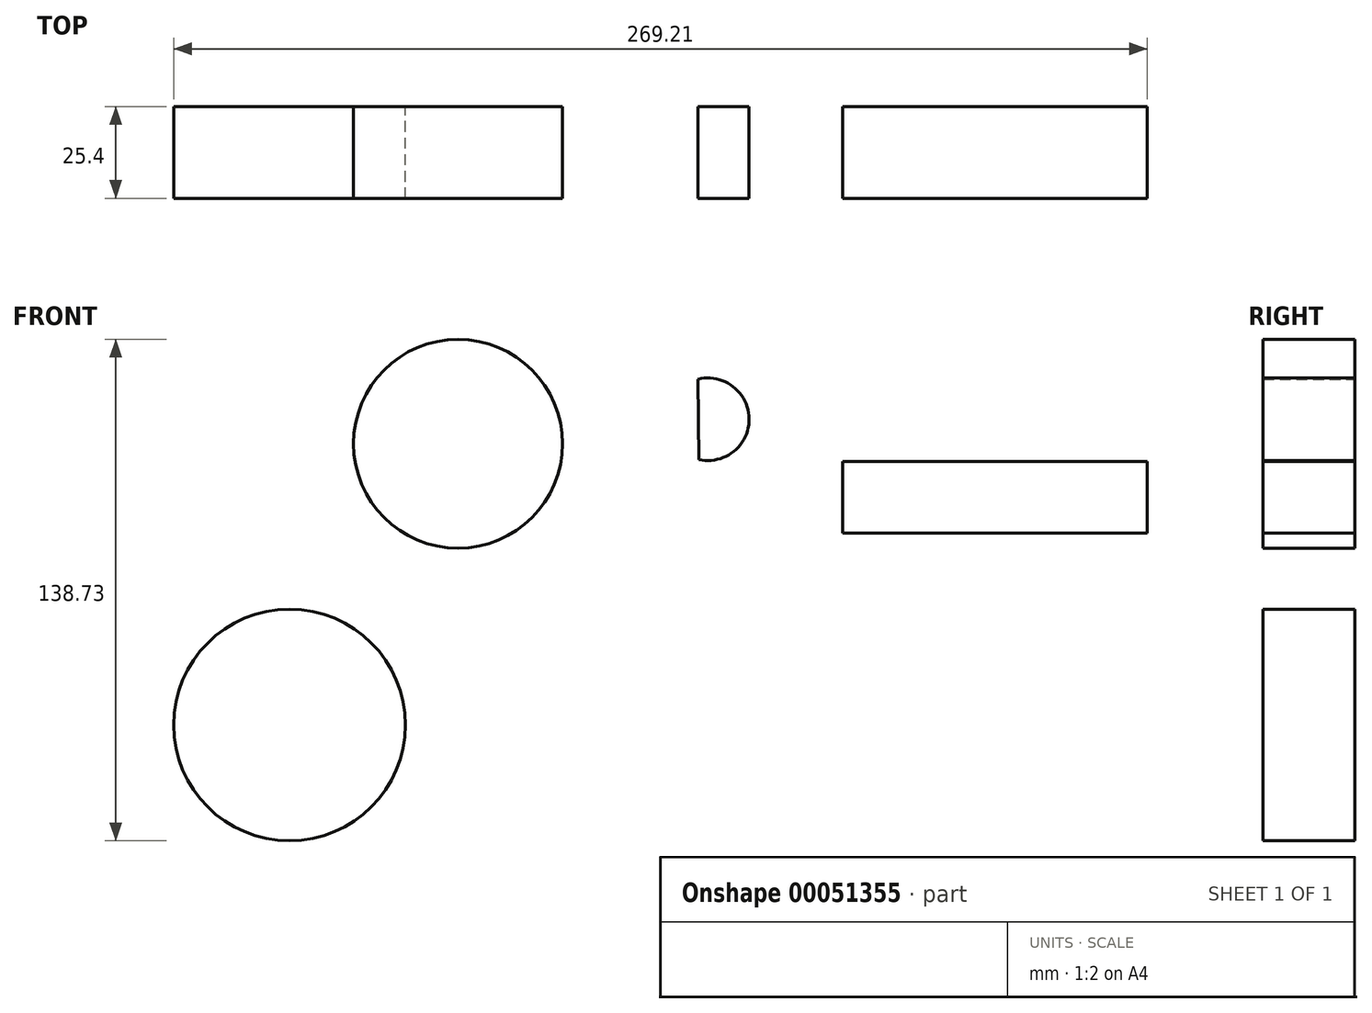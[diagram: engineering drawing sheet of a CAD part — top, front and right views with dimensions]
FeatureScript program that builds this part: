
annotation { "Feature Type Name" : "Feature", "Feature Type Description" : "" }
export const myFeature = defineFeature(function(context is Context, id is Id, definition is map)
    precondition{}
    {
        {
            var Q0;
            Q0=qCreatedBy(makeId("Front.planeOp"),FACE);
            var sketch = newSketch(context, id + "F0", { "sketchPlane" : qUnion([Q0])});
            skCircle(sketch, "E0", {"center": v(-80.38, 43.15) * mm, "radius": 28.9 * mm});
            skLineSegment(sketch, "E1.bottom", {"start": v(25.91, 38.3) * mm, "end": v(110.19, 38.3) * mm});
            skLineSegment(sketch, "E1.top", {"start": v(25.91, 18.45) * mm, "end": v(110.19, 18.45) * mm});
            skLineSegment(sketch, "E1.left", {"start": v(25.91, 38.3) * mm, "end": v(25.91, 18.45) * mm});
            skLineSegment(sketch, "E1.right", {"start": v(110.19, 38.3) * mm, "end": v(110.19, 18.45) * mm});
            skArc(sketch, "E2", {"start": v(-13.83, 38.8) * mm, "mid": v(0.08, 50.06) * mm, "end": v(-14.07, 61.02) * mm});
            skLineSegment(sketch, "E3", {"start": v(-14.07, 61.02) * mm, "end": v(-13.83, 38.8) * mm});
            skCircle(sketch, "E4", {"center": v(-126.98, -34.65) * mm, "radius": 32.04 * mm});
            skSolve(sketch);
        }
        {
            var Q0;
            Q0 = qSketchRegion(id + "F0", true);
            extrude(context, id + "F1", {"entities" : qUnion([Q0]), "depth" : 25.4 * mm});
        }
    });
